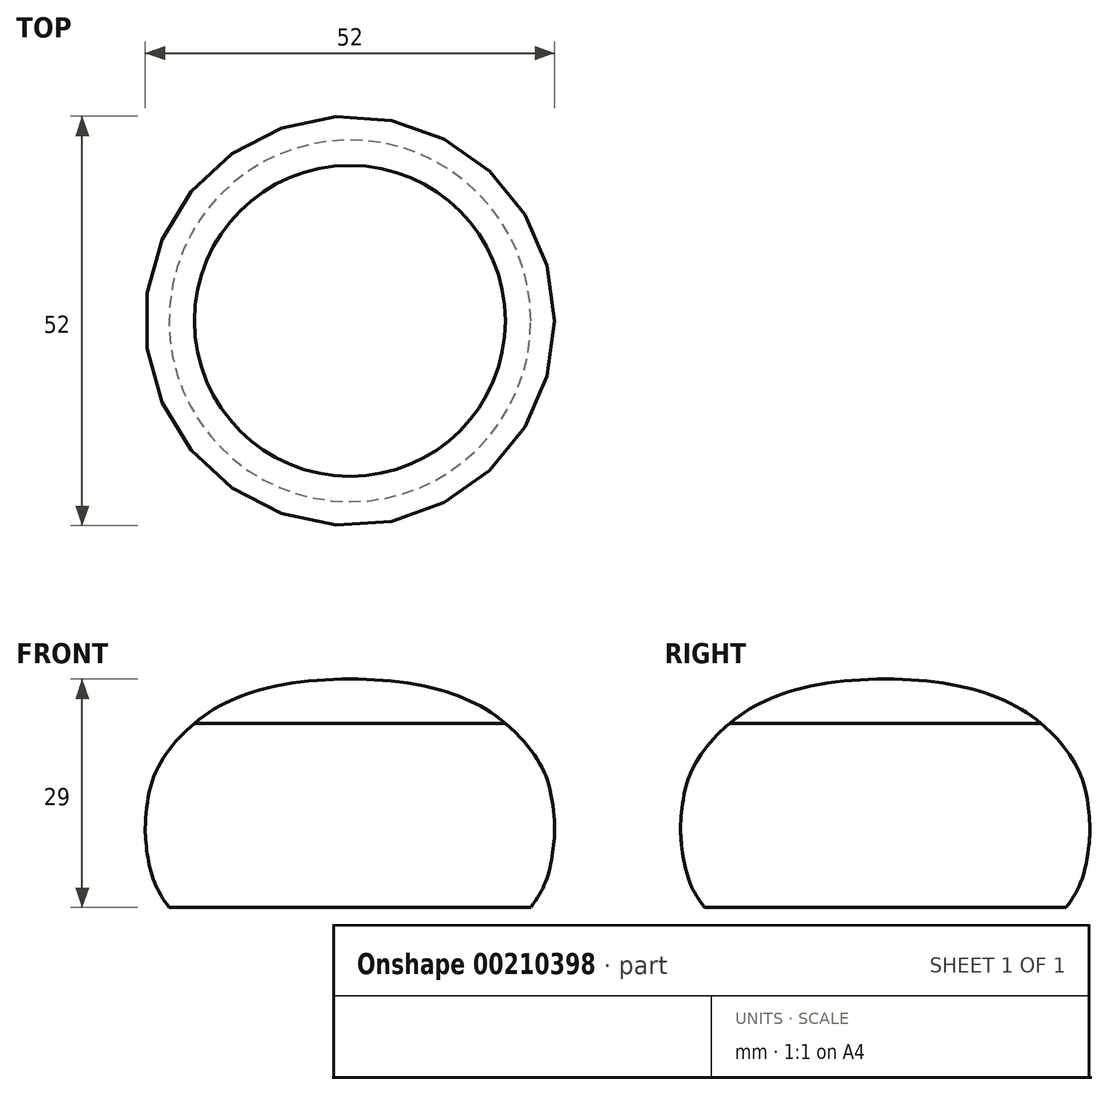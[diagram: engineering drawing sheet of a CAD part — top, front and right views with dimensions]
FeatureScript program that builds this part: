
annotation { "Feature Type Name" : "Feature", "Feature Type Description" : "" }
export const myFeature = defineFeature(function(context is Context, id is Id, definition is map)
    precondition{}
    {
        {
            var Q0;
            Q0=qCreatedBy(makeId("Right.planeOp"),FACE);
            var sketch = newSketch(context, id + "F0", { "sketchPlane" : qUnion([Q0])});
            skFitSpline(sketch, "E0", {"points": [v(0, 19) * mm, v(16.5, 15.6) * mm, v(23.3, 9.56) * mm, v(25.4, 5) * mm, v(26, 0) * mm], "startDerivative": vector(55.77, 0) * mm, "endDerivative": vector(0, -18.91) * mm});
            skFitSpline(sketch, "E1.MirrorCS", {"points": [v(0, 19) * mm, v(-16.5, 15.6) * mm, v(-23.3, 9.56) * mm, v(-25.4, 5) * mm, v(-26, 0) * mm], "startDerivative": vector(-55.77, 0) * mm, "endDerivative": vector(0, -18.91) * mm, "construction": true});
            skFitSpline(sketch, "E2.MirrorCS", {"points": [v(0, -19) * mm, v(-16.5, -15.6) * mm, v(-23.3, -9.56) * mm, v(-25.4, -5) * mm, v(-26, 0) * mm], "startDerivative": vector(-55.77, 0) * mm, "endDerivative": vector(0, 18.91) * mm, "construction": true});
            skFitSpline(sketch, "E3.MirrorCS", {"points": [v(0, -19) * mm, v(16.5, -15.6) * mm, v(23.3, -9.56) * mm, v(25.4, -5) * mm, v(26, 0) * mm], "startDerivative": vector(55.77, 0) * mm, "endDerivative": vector(0, 18.91) * mm});
            skLineSegment(sketch, "E4", {"start": v(0, 19) * mm, "end": v(0, -19) * mm});
            skLineSegment(sketch, "E5", {"start": v(19.75, 13.38) * mm, "end": v(0, 13.38) * mm});
            skSolve(sketch);
        }
        {
            var Q0;
            {var subQ0=sQuery(id+"F0.wireOp",EDGE,"E3.MirrorCS");Q0=makeQuery(id+"F0.imprint","IMPRINT",FACE,{"disambiguationData":[TD([[makeQuery(id+"F0.imprint","IMPRINT",EDGE,{"derivedFrom":subQ0}),1.0]])]});}
            var Q1;
            Q1=sQuery(id+"F0.wireOp",EDGE,"E4");
            revolve(context, id + "F1", {"entities" : qUnion([Q0]), "axis" : qUnion([Q1]), "revolveType" : RevolveType.FULL});
        }
        {
            var Q0;
            {var subQ3=sQuery(id+"F0.wireOp",EDGE,"E5");Q0=makeQuery(id+"F0.imprint","IMPRINT",FACE,{"disambiguationData":[TD([[makeQuery(id+"F0.imprint","IMPRINT",EDGE,{"derivedFrom":subQ3}),-1.0]])]});}
            var Q1;
            Q1=sQuery(id+"F0.wireOp",EDGE,"E4");
            revolve(context, id + "F2", {"entities" : qUnion([Q0]), "axis" : qUnion([Q1]), "revolveType" : RevolveType.FULL});
        }
        {
            var Q0;
            Q0=qCreatedBy(makeId("Right.planeOp"),FACE);
            var sketch = newSketch(context, id + "F3", { "sketchPlane" : qUnion([Q0])});
            skLineSegment(sketch, "E6.bottom", {"start": v(-42.44, -10) * mm, "end": v(53.33, -10) * mm});
            skLineSegment(sketch, "E6.top", {"start": v(-42.44, -57.54) * mm, "end": v(53.33, -57.54) * mm});
            skLineSegment(sketch, "E6.left", {"start": v(-42.44, -10) * mm, "end": v(-42.44, -57.54) * mm});
            skLineSegment(sketch, "E6.right", {"start": v(53.33, -10) * mm, "end": v(53.33, -57.54) * mm});
            skSolve(sketch);
        }
        {
            var Q0;
            Q0=makeQuery(id+"F3.imprint","IMPRINT",FACE,{"disambiguationData":[TD([[makeQuery(id+"F3.imprint","IMPRINT",EDGE,{"derivedFrom":sQuery(id+"F3.wireOp",EDGE,"E6.bottom")}),-1.0]])]});
            extrude(context, id + "F4", {"entities" : qUnion([Q0]), "operationType" : NewBodyOperationType.REMOVE, "endBound" : BoundingType.SYMMETRIC, "oppositeDirection" : true, "depth" : 50 * mm});
        }
    });
